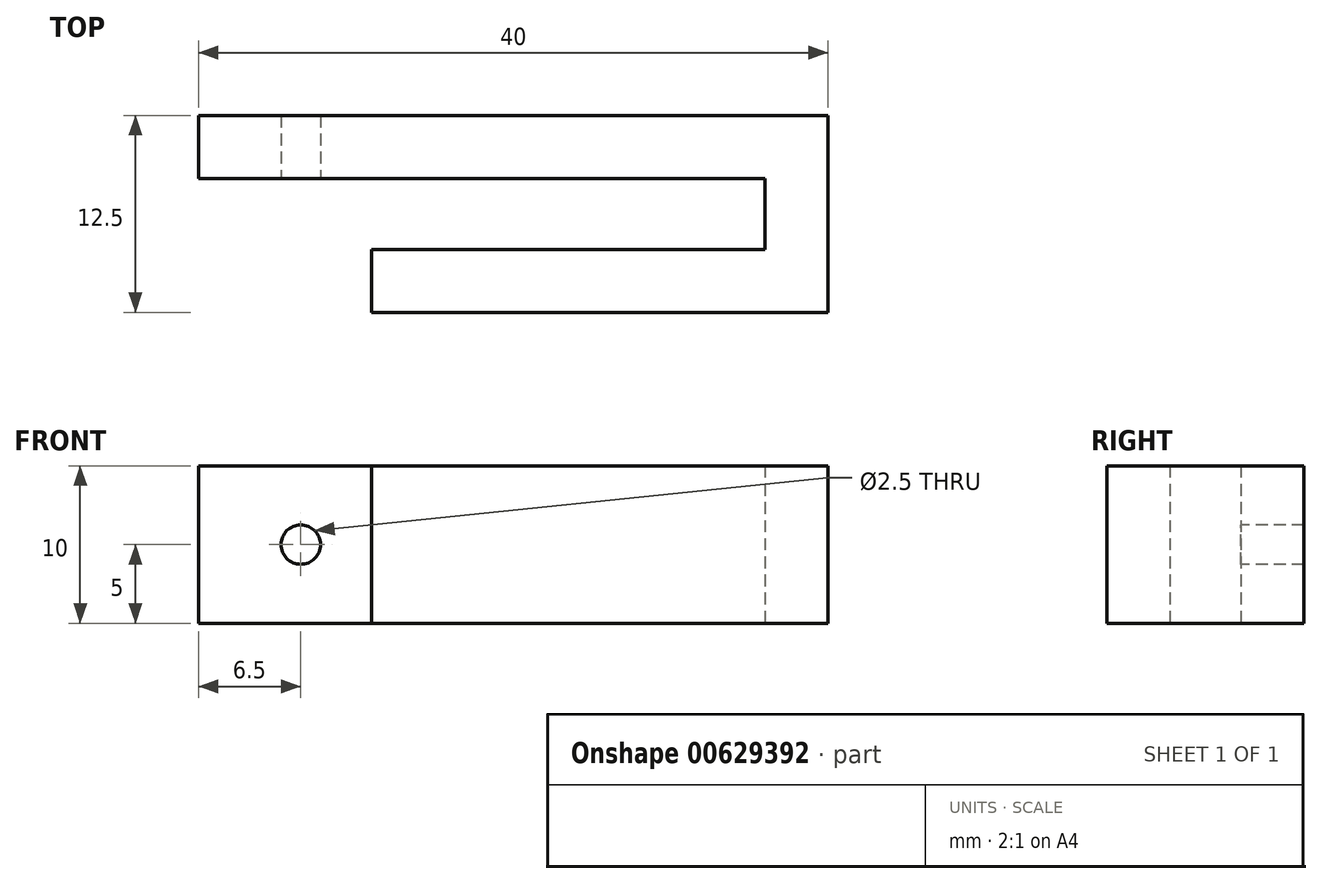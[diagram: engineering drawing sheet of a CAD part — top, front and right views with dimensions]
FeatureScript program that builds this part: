
annotation { "Feature Type Name" : "Feature", "Feature Type Description" : "" }
export const myFeature = defineFeature(function(context is Context, id is Id, definition is map)
    precondition{}
    {
        {
            var Q0;
            Q0=qCreatedBy(makeId("Top.planeOp"),FACE);
            var sketch = newSketch(context, id + "F0", { "sketchPlane" : qUnion([Q0])});
            skLineSegment(sketch, "E0", {"start": v(0, 0) * mm, "end": v(29, 0) * mm});
            skLineSegment(sketch, "E1", {"start": v(29, 0) * mm, "end": v(29, 12.5) * mm});
            skLineSegment(sketch, "E2", {"start": v(29, 12.5) * mm, "end": v(-11, 12.5) * mm});
            skLineSegment(sketch, "E3", {"start": v(-11, 12.5) * mm, "end": v(-11, 8.5) * mm});
            skLineSegment(sketch, "E4", {"start": v(-11, 8.5) * mm, "end": v(25, 8.5) * mm});
            skLineSegment(sketch, "E5", {"start": v(25, 8.5) * mm, "end": v(25, 4) * mm});
            skLineSegment(sketch, "E6", {"start": v(25, 4) * mm, "end": v(0, 4) * mm});
            skLineSegment(sketch, "E7", {"start": v(0, 4) * mm, "end": v(0, 0) * mm});
            skSolve(sketch);
        }
        {
            var Q0;
            Q0 = qSketchRegion(id + "F0", true);
            extrude(context, id + "F1", {"entities" : qUnion([Q0]), "depth" : 10 * mm, "offsetDistance" : 25 * mm});
        }
        {
            var Q0;
            Q0=makeQuery(id+"F1.opExtrude","SWEPT_FACE",FACE,{"disambiguationData":[OSD([sQuery(id+"F0.wireOp",EDGE,"E4")])]});
            var sketch = newSketch(context, id + "F2", { "sketchPlane" : qUnion([Q0])});
            skCircle(sketch, "E8", {"center": v(-4.5, 5) * mm, "radius": 1.25 * mm});
            skSolve(sketch);
        }
        {
            var Q0;
            Q0 = qSketchRegion(id + "F2", true);
            extrude(context, id + "F3", {"entities" : qUnion([Q0]), "operationType" : NewBodyOperationType.REMOVE, "oppositeDirection" : true, "depth" : 25 * mm, "offsetDistance" : 25 * mm});
        }
    });
